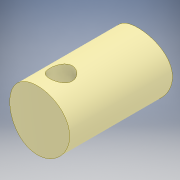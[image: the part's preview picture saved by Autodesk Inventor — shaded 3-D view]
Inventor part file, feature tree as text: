
AUTODESK INVENTOR PART (.ipt)
format: ipt  version: 2018 (Build 220112000, 112)  size: 119,296 bytes
history: native  units: mm
features: extrude x2, sketch x2
ambient origin geometry x8: Origin, YZ Plane, XZ Plane, XY Plane, X Axis, Y Axis, Z Axis, Center Point
bodies: Body1 (feature_tree)
feature tree (4):
  extrude  "Extrusion2"  Depth=42.4mm TaperAngle=0.0deg
  extrude  "Extrusion3"  Depth=42.4mm TaperAngle=0.0deg
  sketch  "Sketch2"  dims[d10=12.7mm d11=42.4mm d12=0.0mm]
  sketch  "Sketch3"  dims[d13=42.164mm d14=42.4mm d15=0.0mm d16=4.7625mm d17=5.0mm]
